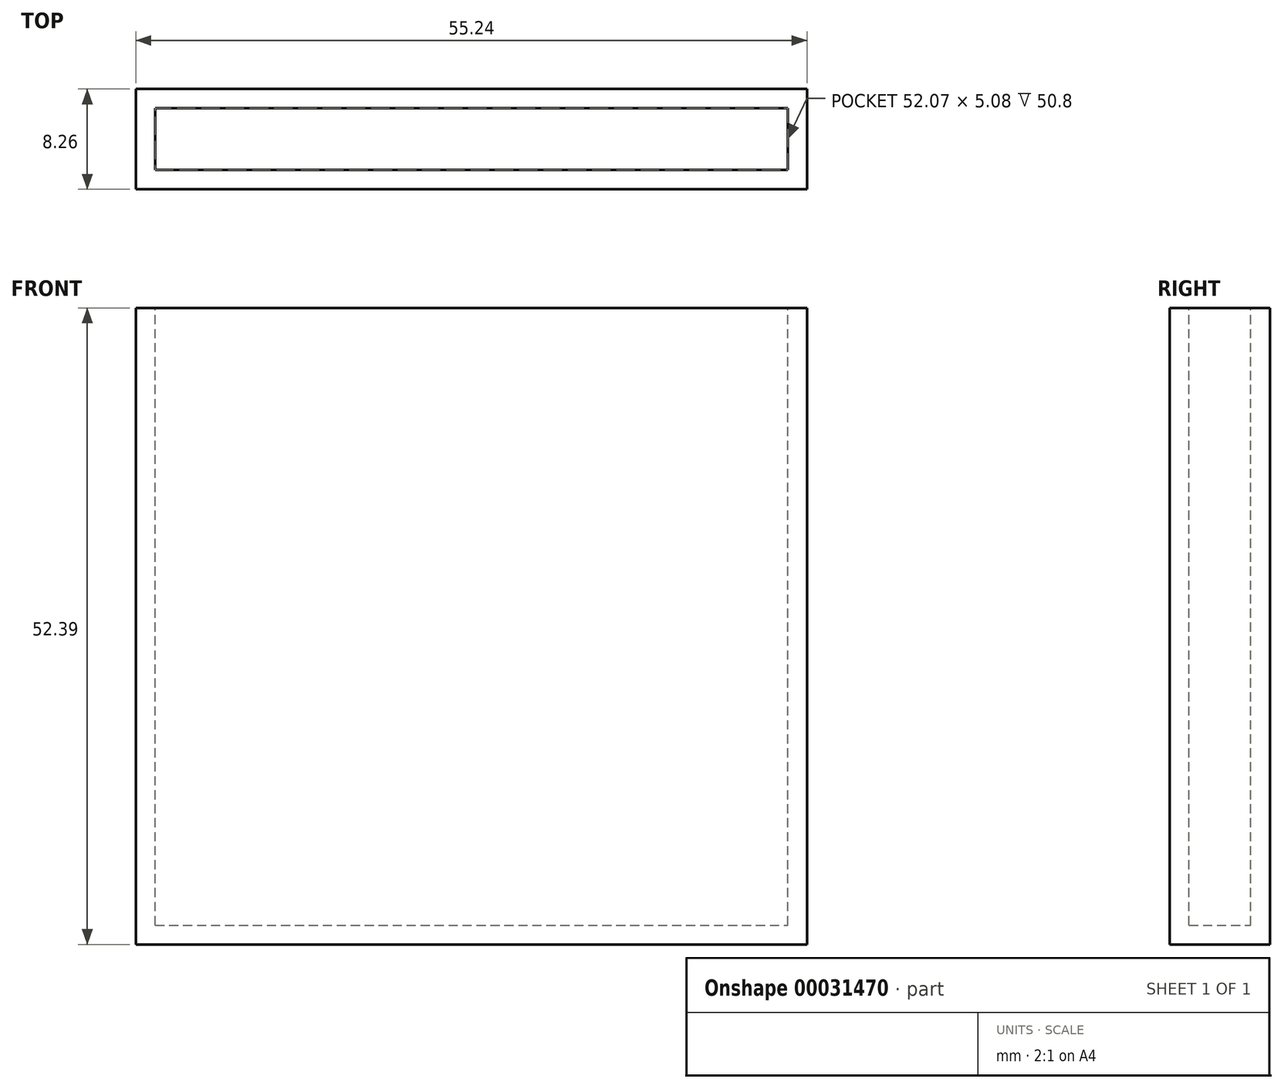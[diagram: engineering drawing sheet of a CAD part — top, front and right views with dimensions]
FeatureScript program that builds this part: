
annotation { "Feature Type Name" : "Feature", "Feature Type Description" : "" }
export const myFeature = defineFeature(function(context is Context, id is Id, definition is map)
    precondition{}
    {
        {
            var Q0;
            Q0=qCreatedBy(makeId("Top.planeOp"),FACE);
            var sketch = newSketch(context, id + "F0", { "sketchPlane" : qUnion([Q0])});
            skLineSegment(sketch, "E0.rect.bottom", {"start": v(-27.62, -4.13) * mm, "end": v(27.62, -4.13) * mm});
            skLineSegment(sketch, "E0.rect.top", {"start": v(-27.62, 4.13) * mm, "end": v(27.62, 4.13) * mm});
            skLineSegment(sketch, "E0.rect.left", {"start": v(-27.62, -4.13) * mm, "end": v(-27.62, 4.13) * mm});
            skLineSegment(sketch, "E0.rect.right", {"start": v(27.62, -4.13) * mm, "end": v(27.62, 4.13) * mm});
            skPoint(sketch, "E0.rect.middle", {"position": v(0, 0) * mm});
            skLineSegment(sketch, "E1.rect.bottom", {"start": v(-26.04, -2.54) * mm, "end": v(26.04, -2.54) * mm});
            skLineSegment(sketch, "E1.rect.top", {"start": v(-26.04, 2.54) * mm, "end": v(26.04, 2.54) * mm});
            skLineSegment(sketch, "E1.rect.left", {"start": v(-26.04, -2.54) * mm, "end": v(-26.04, 2.54) * mm});
            skLineSegment(sketch, "E1.rect.right", {"start": v(26.04, -2.54) * mm, "end": v(26.04, 2.54) * mm});
            skSolve(sketch);
        }
        {
            var Q0;
            Q0=makeQuery(id+"F0.imprint","IMPRINT",FACE,{"disambiguationData":[TD([[makeQuery(id+"F0.imprint","IMPRINT",EDGE,{"derivedFrom":sQuery(id+"F0.wireOp",EDGE,"E0.rect.bottom")}),1.0]])]});
            var Q1;
            Q1=makeQuery(id+"F0.imprint","IMPRINT",FACE,{"disambiguationData":[TD([[makeQuery(id+"F0.imprint","IMPRINT",EDGE,{"derivedFrom":sQuery(id+"F0.wireOp",EDGE,"E1.rect.bottom")}),1.0]])]});
            extrude(context, id + "F1", {"entities" : qUnion([Q0, Q1]), "oppositeDirection" : true, "depth" : 52.4 * mm});
        }
        {
            var Q0;
            Q0=makeQuery(id+"F0.imprint","IMPRINT",FACE,{"disambiguationData":[TD([[makeQuery(id+"F0.imprint","IMPRINT",EDGE,{"derivedFrom":sQuery(id+"F0.wireOp",EDGE,"E1.rect.bottom")}),1.0]])]});
            extrude(context, id + "F2", {"entities" : qUnion([Q0]), "operationType" : NewBodyOperationType.REMOVE, "oppositeDirection" : true, "depth" : 50.8 * mm});
        }
    });
